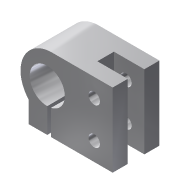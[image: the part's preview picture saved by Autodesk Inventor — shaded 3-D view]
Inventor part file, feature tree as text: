
AUTODESK INVENTOR PART (.ipt)
format: ipt  version: 2015 (Build 190159000, 159)  size: 176,640 bytes
history: native  units: mm
features: sketch x4, extrude x3, revolve x1
ambient origin geometry x8: Origin, YZ Plane, XZ Plane, XY Plane, X Axis, Y Axis, Z Axis, Center Point
bodies: Solid1 (feature_tree)
feature tree (8):
  extrude  "Extrusion1"  Depth=40.0mm
  extrude  "Extrusion2"  Depth=10.0mm
  revolve  "Revolution2"  [1 undecoded]
  extrude  "Extrusion3"  Depth=45.5mm
  sketch  "Sketch1"  dims[d0=50.0mm d1=40.0mm]
  sketch  "Sketch2"  dims[d2=10.0mm d3=10.0mm]
  sketch  "Sketch6"  dims[d4=20.0mm d5=6.2mm]
  sketch  "Sketch7"  dims[d6=6.2mm d7=45.5mm d8=35.5mm d9=4.5mm d10=4.5mm d13=12.5mm d14=12.5mm d15=2.0mm d16=25.4mm d17=0.0mm d18=8.2mm d19=16.5mm d20=9.0mm d21=25.4mm d22=0.0mm d23=10.0mm d35=14.835299mm d36=10.0mm d37=14.835299mm d43=30.0mm d44=90.0deg d45=30.0mm d47=30.0mm d48=16.580628mm d49=9.5mm d50=90.0deg d51=10.0mm d52=0.0mm]
note: 1 required parameter value undecoded (feature->parameter linkage not recoverable at this tier; creation-order binding heuristic only, values carry confidence <= 0.55)
